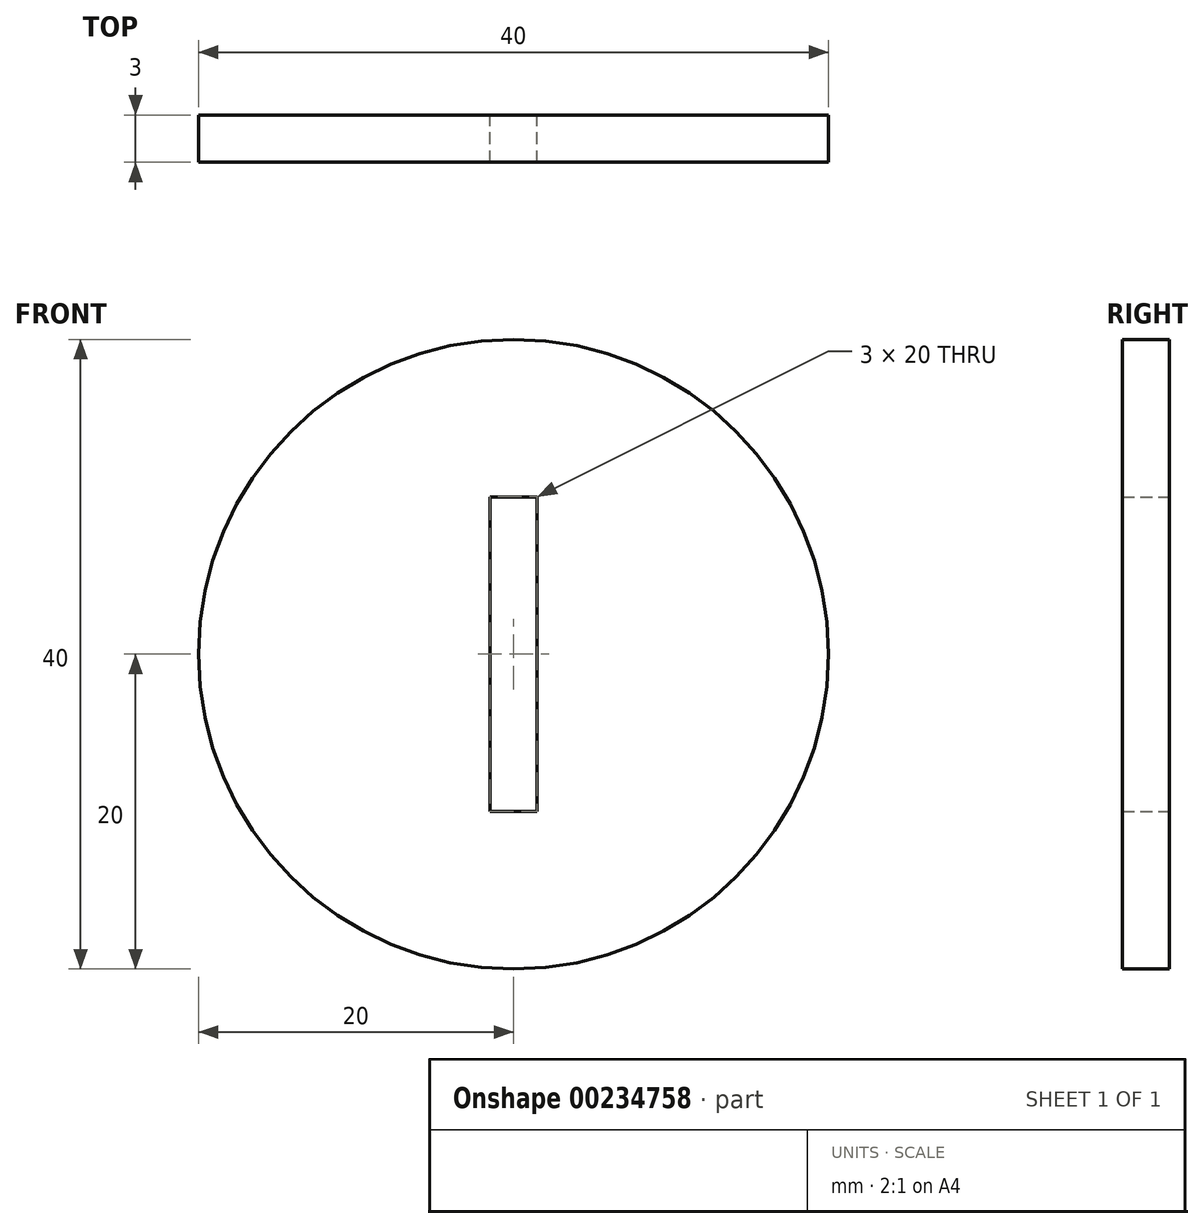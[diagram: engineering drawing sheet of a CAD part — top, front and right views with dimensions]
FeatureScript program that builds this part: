
annotation { "Feature Type Name" : "Feature", "Feature Type Description" : "" }
export const myFeature = defineFeature(function(context is Context, id is Id, definition is map)
    precondition{}
    {
        {
            var Q0;
            Q0=qCreatedBy(makeId("Front.planeOp"),FACE);
            var sketch = newSketch(context, id + "F0", { "sketchPlane" : qUnion([Q0])});
            skCircle(sketch, "E0", {"center": v(0, 0) * mm, "radius": 20 * mm});
            skLineSegment(sketch, "E1.bottom", {"start": v(1.5, 10) * mm, "end": v(-1.5, 10) * mm});
            skLineSegment(sketch, "E1.top", {"start": v(1.5, -10) * mm, "end": v(-1.5, -10) * mm});
            skLineSegment(sketch, "E1.left", {"start": v(1.5, 10) * mm, "end": v(1.5, -10) * mm});
            skLineSegment(sketch, "E1.right", {"start": v(-1.5, 10) * mm, "end": v(-1.5, -10) * mm});
            skSolve(sketch);
        }
        {
            var Q0;
            Q0=makeQuery(id+"F0.imprint","IMPRINT",FACE,{"disambiguationData":[TD([[makeQuery(id+"F0.imprint","IMPRINT",EDGE,{"derivedFrom":sQuery(id+"F0.wireOp",EDGE,"E0")}),1.0]])]});
            extrude(context, id + "F1", {"entities" : qUnion([Q0]), "depth" : 3 * mm});
        }
    });
